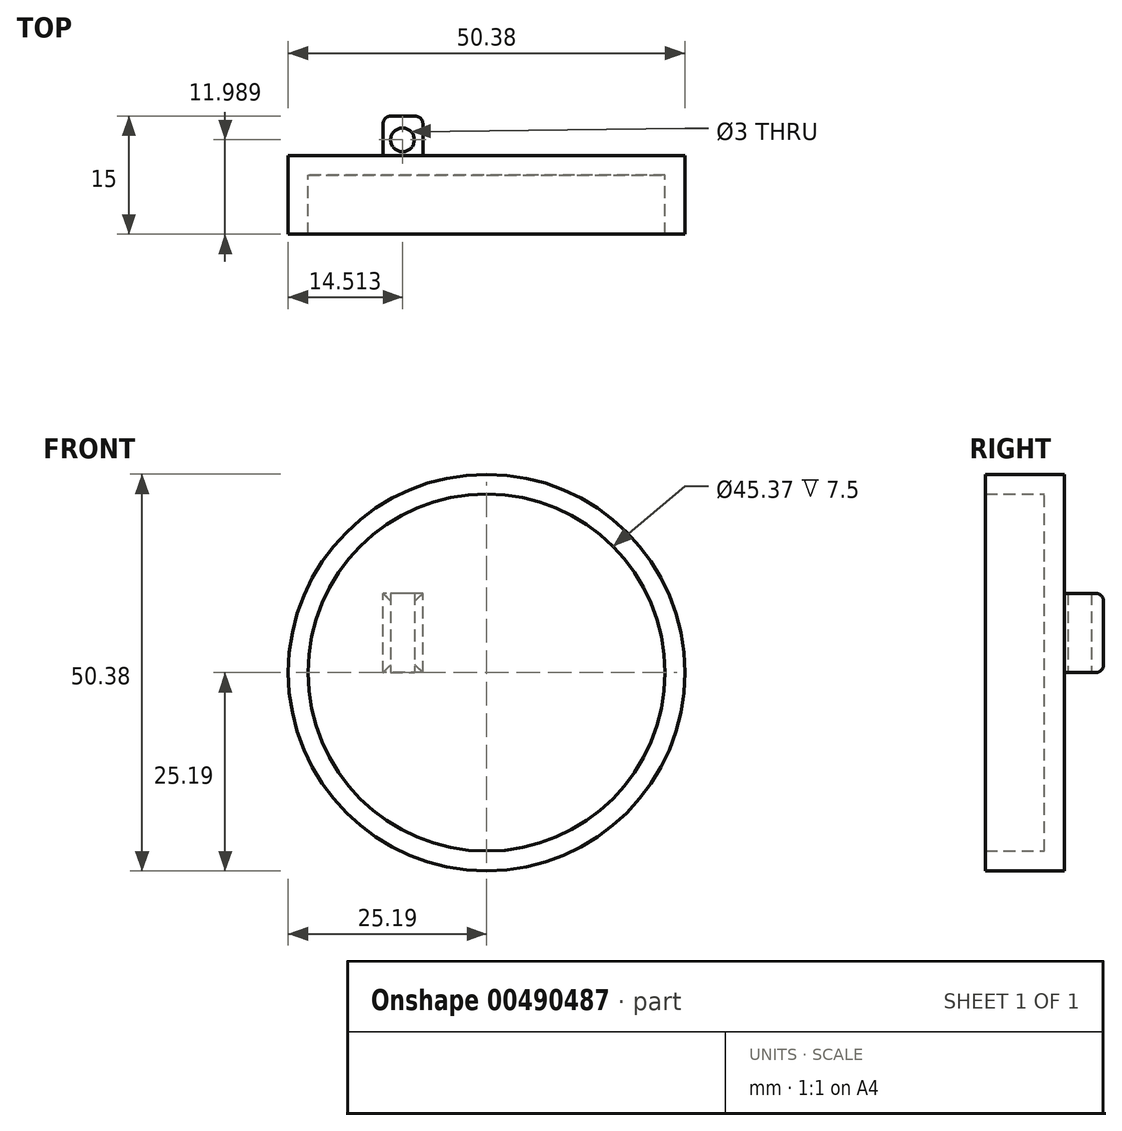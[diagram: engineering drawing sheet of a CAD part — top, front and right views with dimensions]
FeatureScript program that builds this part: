
annotation { "Feature Type Name" : "Feature", "Feature Type Description" : "" }
export const myFeature = defineFeature(function(context is Context, id is Id, definition is map)
    precondition{}
    {
        {
            var Q0;
            Q0=qCreatedBy(makeId("Front.planeOp"),FACE);
            var sketch = newSketch(context, id + "F0", { "sketchPlane" : qUnion([Q0])});
            skCircle(sketch, "E0", {"center": v(0, 0) * mm, "radius": 25.19 * mm});
            skSolve(sketch);
        }
        {
            var Q0;
            Q0 = qSketchRegion(id + "F0", true);
            var Q1;
            Q1=makeQuery(id+"F0.imprint","IMPRINT",FACE,{"disambiguationData":[TD([[makeQuery(id+"F0.imprint","IMPRINT",EDGE,{"derivedFrom":sQuery(id+"F0.wireOp",EDGE,"E0")}),1.0]])]});
            extrude(context, id + "F1", {"entities" : qUnion([Q0, Q1]), "depth" : 10 * mm});
        }
        {
            var Q0;
            Q0=makeQuery(id+"F1.opExtrude","CAP_FACE",FACE,{"disambiguationData":[OSD([sQuery(id+"F0.wireOp",EDGE,"E0")])],"isStart":false});
            shell(context, id + "F2", {"entities" : qUnion([Q0]), "thickness" : 2.5 * mm});
        }
        {
            var Q0;
            Q0=makeQuery(id+"F1.opExtrude","CAP_FACE",FACE,{"disambiguationData":[OSD([sQuery(id+"F0.wireOp",EDGE,"E0")])],"isStart":true});
            var sketch = newSketch(context, id + "F3", { "sketchPlane" : qUnion([Q0])});
            skLineSegment(sketch, "E1.bottom", {"start": v(8.08, 0) * mm, "end": v(13.16, 0) * mm});
            skLineSegment(sketch, "E1.top", {"start": v(8.08, 10.07) * mm, "end": v(13.16, 10.07) * mm});
            skLineSegment(sketch, "E1.left", {"start": v(8.08, 0) * mm, "end": v(8.08, 10.07) * mm});
            skLineSegment(sketch, "E1.right", {"start": v(13.16, 0) * mm, "end": v(13.16, 10.07) * mm});
            skSolve(sketch);
        }
        {
            var Q0;
            Q0 = qSketchRegion(id + "F3", true);
            extrude(context, id + "F4", {"entities" : qUnion([Q0]), "operationType" : NewBodyOperationType.ADD, "depth" : 5 * mm});
        }
        {
            var Q0;
            Q0=makeQuery(id+"F4.opExtrude","CAP_FACE",FACE,{"disambiguationData":[OSD([sQuery(id+"F3.wireOp",EDGE,"E1.bottom"),sQuery(id+"F3.wireOp",EDGE,"E1.top"),sQuery(id+"F3.wireOp",EDGE,"E1.left"),sQuery(id+"F3.wireOp",EDGE,"E1.right")])],"isStart":false});
            fillet(context, id + "F5", {"entities" : qUnion([Q0]), "radius" : 1 * mm, "tangentPropagation" : true, "allowEdgeOverflow" : false});
        }
        {
            var Q0;
            Q0=qCreatedBy(makeId("Top.planeOp"),FACE);
            var sketch = newSketch(context, id + "F6", { "sketchPlane" : qUnion([Q0])});
            skCircle(sketch, "E2", {"center": v(-10.68, 1.99) * mm, "radius": 1.5 * mm});
            skSolve(sketch);
        }
        {
            var Q0;
            Q0=sQuery(id+"F6.wireOp",VERTEX,"E2.center");
            var Q1;
            Q1=makeQuery(id+"F1.opExtrude","SWEPT_BODY",BODY,{"disambiguationData":[OSD([sQuery(id+"F0.wireOp",EDGE,"E0")])]});
            hole(context, id + "F7", {"style" : HoleStyle.SIMPLE, "endStyle" : HoleEndStyle.THROUGH, "oppositeDirection" : true, "holeDiameter" : 3 * mm, "isTappedThrough" : true, "tappedDepth" : 12 * mm, "tapClearance" : 3, "locations" : qUnion([Q0]), "scope" : qUnion([Q1])});
        }
    });
